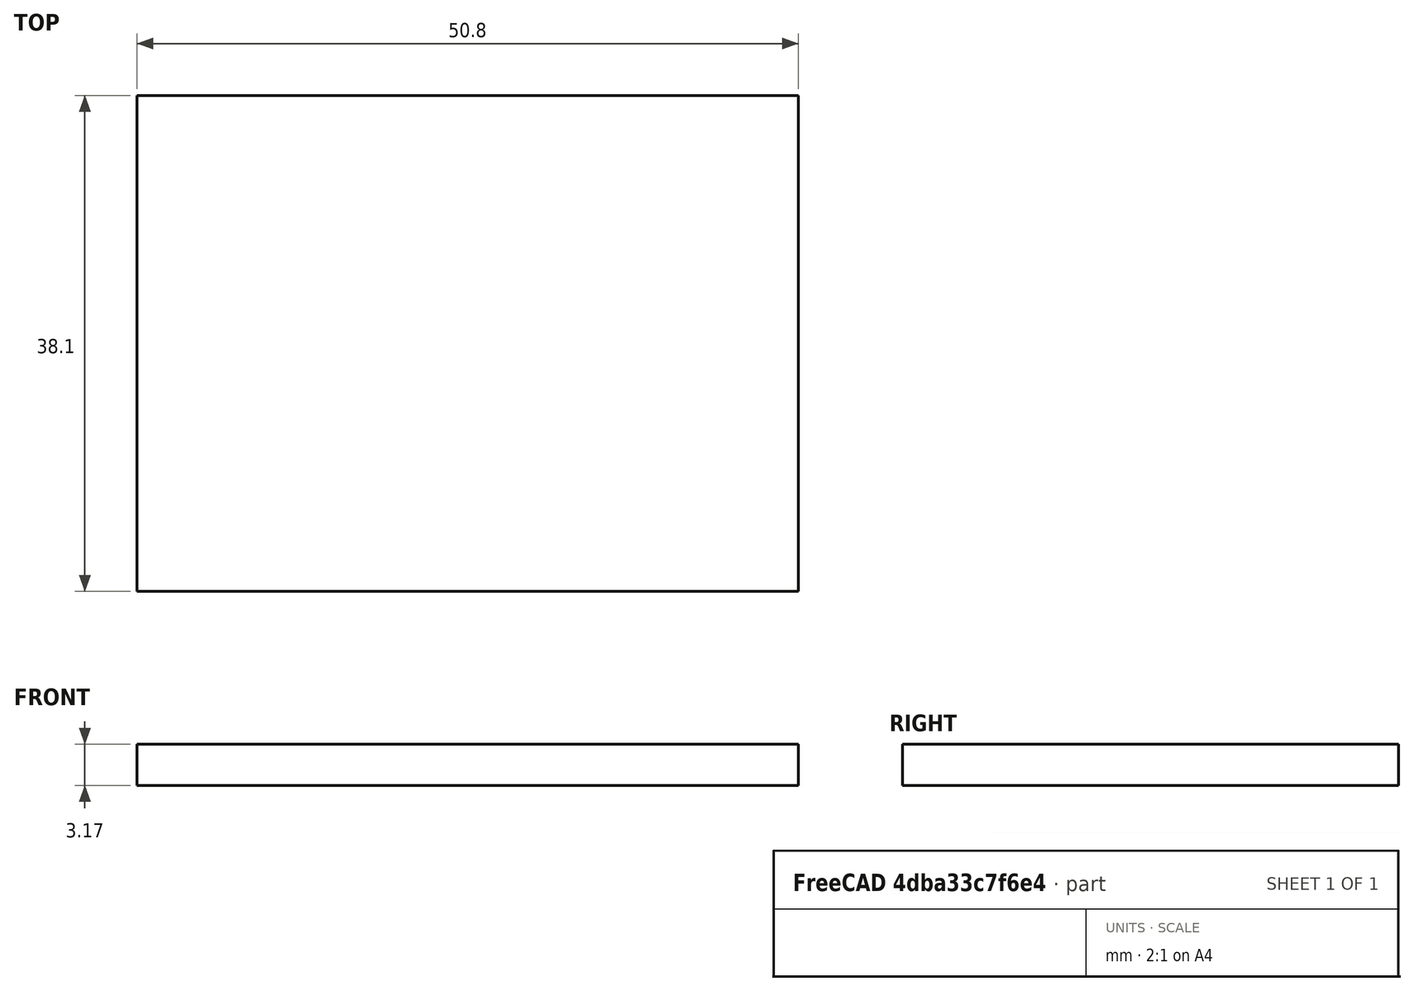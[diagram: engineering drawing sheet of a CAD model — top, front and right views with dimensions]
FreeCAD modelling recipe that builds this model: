
FCSTD DOCUMENT  (FreeCAD 0.20R29603 (Git))
Label: OneEighthInchSpacer
License: All rights reserved
LicenseURL: http://en.wikipedia.org/wiki/All_rights_reserved
objects: Sketcher::SketchObject×1, PartDesign::Pad×1, PartDesign::Body×1, App::Part×1
note: 4 computed .brp shape members not serialized (recipe doc carries the construction recipe); baked Part::Feature solids carry a one-line shape summary decoded from their .brp

FEATURE [Sketcher::SketchObject] Sketch
  FullyConstrained = true
  MapMode = 5
  Support = -> [XY_Plane001]
  expr: Constraints[10] = 25.4 * 2
  expr: Constraints[11] = 25.4 + 25.4 / 2
  sketch-geometry (5):
    g0: LineSegment StartX=-25.4 StartY=19.05 StartZ=0 EndX=-25.4 EndY=-19.05 EndZ=0
    g1: LineSegment StartX=-25.4 StartY=-19.05 StartZ=0 EndX=25.4 EndY=-19.05 EndZ=0
    g2: LineSegment StartX=25.4 StartY=-19.05 StartZ=0 EndX=25.4 EndY=19.05 EndZ=0
    g3: LineSegment StartX=25.4 StartY=19.05 StartZ=0 EndX=-25.4 EndY=19.05 EndZ=0
    g4: GeomPoint X=0 Y=0 Z=0
  constraints (12):
    c: Coincident(g0,g1)
    c: Coincident(g1,g2)
    c: Coincident(g2,g3)
    c: Coincident(g3,g0)
    c: Horizontal(g1)
    c: Horizontal(g3)
    c: Vertical(g0)
    c: Vertical(g2)
    c: Symmetric(g1,g0,g4)
    c: Coincident(g4,g-1)
    c: DistanceX(g3,g3) = 50.8
    c: DistanceY(g2,g2) = 38.1
FEATURE [PartDesign::Pad] Pad
  Direction = (0,0,1)
  Length = 3.175
  Length2 = 10
  Profile = -> Sketch
  ReferenceAxis = -> Sketch [N_Axis]
  Type = 0
FEATURE [PartDesign::Body] Body
  Group = -> [Sketch,Pad]
  Origin = -> Origin001
  Tip = -> Pad
FEATURE [App::Part] Part
  Group = -> [Body]
  Origin = -> Origin
